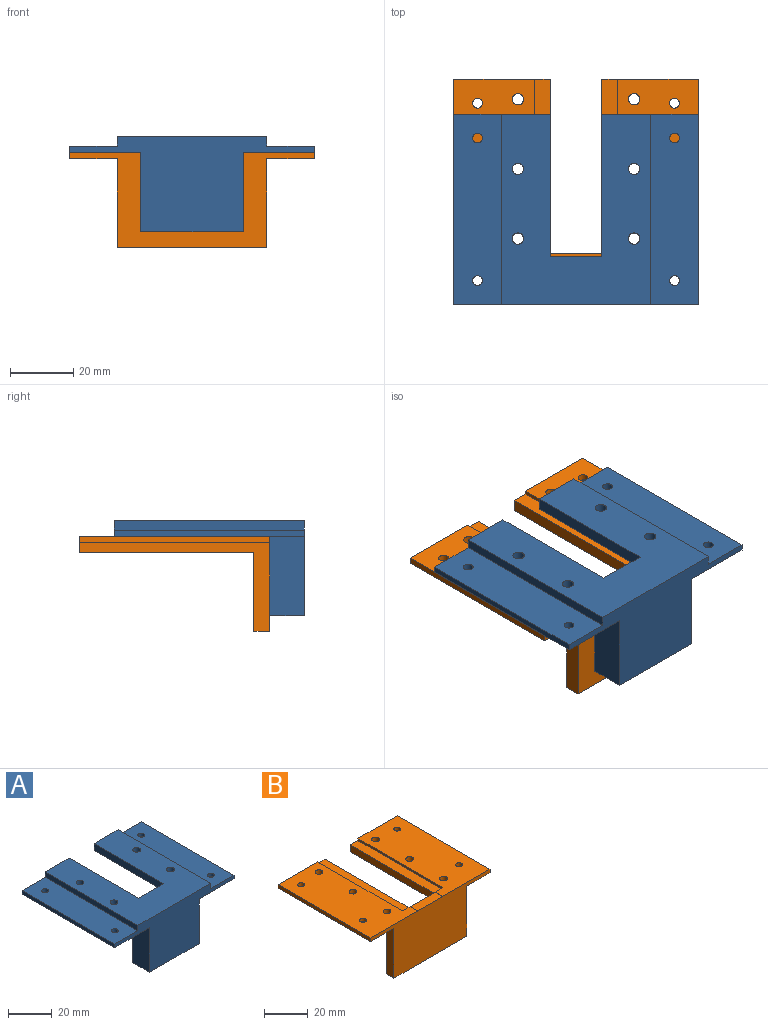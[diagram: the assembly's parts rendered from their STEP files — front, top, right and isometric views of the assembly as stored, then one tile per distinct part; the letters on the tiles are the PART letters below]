
ASSEMBLY  parts=2 mates=1
PART A: 33 faces, bbox 77.2x60x30 mm
  f0: plane 60x3mm, normal (-1,0,0), area 180mm2, adj f4,f5,f7,f29
  f1: plane 60x3mm, normal (1,0,0), area 180mm2, adj f4,f6,f7,f25
  f2: plane 60x25.5mm, normal (0,0,-1), area 1461.5mm2, adj f6,f7,f8,f15,f18,f21,f22,f26
  f3: plane 60x25.5mm, normal (0,0,-1), area 1461.5mm2, adj f5,f7,f10,f16,f17,f23,f24,f30
  f4: plane 60x47.2mm, normal (0,0,1), area 2062.3mm2, adj f0,f1,f5,f6,f7,f12,f13,f14
  f5: plane 30.5x5mm, normal (0,1,0), area 102mm2, adj f0,f3,f4,f10,f11,f14,f29,f30
  f6: plane 30.5x5mm, normal (0,1,0), area 102mm2, adj f1,f2,f4,f8,f11,f12,f25,f26
  f7: plane 77.2x30mm, normal (0,-1,0), area 1101mm2, adj f0,f1,f2,f3,f4,f19,f22,f23
  f8: plane 59x26.1mm, normal (-1,0,0), area 192.5mm2, adj f2,f6,f9,f11,f19,f20,f21
  f9: plane 26.2x1.1mm, normal (0,1,0), area 28.8mm2, adj f8,f10,f11,f20
  f10: plane 59x26.1mm, normal (1,0,0), area 192.5mm2, adj f3,f5,f9,f11,f19,f20,f24
  f11: plane 50x26.2mm, normal (0,0,-1), area 581mm2, adj f5,f6,f8,f9,f10,f12,f13,f14
  f12: plane 45x3.9mm, normal (-1,0,0), area 175.5mm2, adj f4,f6,f11,f13
  f13: plane 16.2x3.9mm, normal (0,1,0), area 63.2mm2, adj f4,f11,f12,f14
  f14: plane 45x3.9mm, normal (1,0,0), area 175.5mm2, adj f4,f5,f11,f13
  f15: cylinder r=1.8mm len=5mm, axis (0,0,-1), area 56.5mm2, adj f2,f4
  f16: cylinder r=1.8mm len=5mm, axis (0,0,-1), area 56.5mm2, adj f3,f4
  f17: cylinder r=1.8mm len=5mm, axis (0,0,-1), area 56.5mm2, adj f3,f4
  f18: cylinder r=1.8mm len=5mm, axis (0,0,-1), area 56.5mm2, adj f2,f4
  f19: plane 32.2x11mm, normal (0,0,-1), area 92.2mm2, adj f7,f8,f10,f20,f21,f22,f23,f24
  f20: plane 26.2x25mm, normal (0,0.94,-0.34), area 696.2mm2, adj f8,f9,f10,f19
  f21: plane 25x3mm, normal (0,1,0), area 75mm2, adj f2,f8,f19,f22
  f22: plane 25x11mm, normal (1,0,0), area 275mm2, adj f2,f7,f19,f21
  f23: plane 25x11mm, normal (-1,0,0), area 275mm2, adj f3,f7,f19,f24
  f24: plane 25x3mm, normal (0,1,0), area 75mm2, adj f3,f10,f19,f23
  f25: plane 60x15mm, normal (0,0,1), area 884.9mm2, adj f1,f6,f7,f26,f27,f28
  f26: plane 60x2mm, normal (1,0,0), area 120mm2, adj f2,f6,f7,f25
  f27: cylinder r=1.55mm len=3.1mm, axis (0,0,1), area 19.5mm2, adj f2,f25
  f28: cylinder r=1.55mm len=3.1mm, axis (0,0,1), area 19.5mm2, adj f2,f25
  f29: plane 60x15mm, normal (0,0,1), area 884.9mm2, adj f0,f5,f7,f30,f31,f32
  f30: plane 60x2mm, normal (-1,0,0), area 120mm2, adj f3,f5,f7,f29
  f31: cylinder r=1.55mm len=3.1mm, axis (0,0,1), area 19.5mm2, adj f3,f29
  f32: cylinder r=1.55mm len=3.1mm, axis (0,0,1), area 19.5mm2, adj f3,f29
PART B: 76 faces, bbox 77.2x60x30 mm
  f0: plane 60x28mm, normal (1,0,0), area 305mm2, adj f4,f12,f15,f17,f64,f72
  f1: plane 60x28mm, normal (-1,0,0), area 305mm2, adj f3,f14,f15,f17,f64,f68
  f2: plane 60x30.5mm, normal (0,0,1), area 1509.4mm2, adj f5,f6,f7,f14,f15,f16,f17,f66
  f3: plane 55x15.5mm, normal (0,0,-1), area 742.7mm2, adj f1,f14,f17,f20,f44,f45,f46,f47
  f4: plane 55x15.5mm, normal (0,0,-1), area 742.7mm2, adj f0,f12,f17,f21,f22,f23,f24,f25
  f5: cylinder r=1.8mm len=3.6mm, axis (0,0,1), area 28.3mm2, adj f2,f57
  f6: cylinder r=1.8mm len=3.6mm, axis (0,0,1), area 28.3mm2, adj f2,f50
  f7: cylinder r=1.8mm len=3.6mm, axis (0,0,1), area 28.3mm2, adj f2,f43
  f8: cylinder r=1.8mm len=3.6mm, axis (0,0,1), area 28.3mm2, adj f11,f42
  f9: cylinder r=1.8mm len=3.6mm, axis (0,0,1), area 28.3mm2, adj f11,f35
  f10: cylinder r=1.8mm len=3.6mm, axis (0,0,1), area 28.3mm2, adj f11,f28
  f11: plane 60x30.5mm, normal (0,0,1), area 1509.4mm2, adj f8,f9,f10,f12,f15,f17,f18,f65
  f12: plane 30.5x5mm, normal (0,1,0), area 102mm2, adj f0,f4,f11,f13,f18,f21,f72,f73
  f13: plane 55x5mm, normal (0,0,1), area 275mm2, adj f12,f17,f18,f21
  f14: plane 30.5x5mm, normal (0,1,0), area 102mm2, adj f1,f2,f3,f16,f19,f20,f68,f69
  f15: plane 77.2x30mm, normal (0,-1,0), area 1474.4mm2, adj f0,f1,f2,f11,f64,f65,f66,f67
  f16: plane 55x1.1mm, normal (1,0,0), area 60.5mm2, adj f2,f14,f17,f19
  f17: plane 47.2x30mm, normal (0,1,0), area 1270.4mm2, adj f0,f1,f2,f3,f4,f11,f13,f16
  f18: plane 55x1.1mm, normal (-1,0,0), area 60.5mm2, adj f11,f12,f13,f17
  f19: plane 55x5mm, normal (0,0,1), area 275mm2, adj f14,f16,f17,f20
  f20: plane 55x3.9mm, normal (1,0,0), area 214.5mm2, adj f3,f14,f17,f19
  f21: plane 55x3.9mm, normal (-1,0,0), area 214.5mm2, adj f4,f12,f13,f17
  f22: plane 3.25x2.5mm, normal (0.5,-0.87,0), area 9.4mm2, adj f4,f23,f27,f28
  f23: plane 3.25x2.5mm, normal (-0.5,-0.87,0), area 9.4mm2, adj f4,f22,f24,f28
  f24: plane 3.75x2.5mm, normal (-1,0,0), area 9.4mm2, adj f4,f23,f25,f28
  f25: plane 3.25x2.5mm, normal (-0.5,0.87,0), area 9.4mm2, adj f4,f24,f26,f28
  f26: plane 3.25x2.5mm, normal (0.5,0.87,0), area 9.4mm2, adj f4,f25,f27,f28
  f27: plane 3.75x2.5mm, normal (1,0,0), area 9.4mm2, adj f4,f22,f26,f28
  f28: plane 7.51x6.5mm, normal (0,0,-1), area 26.4mm2, adj f10,f22,f23,f24,f25,f26,f27
  f29: plane 3.25x2.5mm, normal (0.5,-0.87,0), area 9.4mm2, adj f4,f30,f34,f35
  f30: plane 3.25x2.5mm, normal (-0.5,-0.87,0), area 9.4mm2, adj f4,f29,f31,f35
  f31: plane 3.75x2.5mm, normal (-1,0,0), area 9.4mm2, adj f4,f30,f32,f35
  f32: plane 3.25x2.5mm, normal (-0.5,0.87,0), area 9.4mm2, adj f4,f31,f33,f35
  f33: plane 3.25x2.5mm, normal (0.5,0.87,0), area 9.4mm2, adj f4,f32,f34,f35
  f34: plane 3.75x2.5mm, normal (1,0,0), area 9.4mm2, adj f4,f29,f33,f35
  f35: plane 7.51x6.5mm, normal (0,0,-1), area 26.4mm2, adj f9,f29,f30,f31,f32,f33,f34
  f36: plane 3.25x2.5mm, normal (0.5,-0.87,0), area 9.4mm2, adj f4,f37,f41,f42
  f37: plane 3.25x2.5mm, normal (-0.5,-0.87,0), area 9.4mm2, adj f4,f36,f38,f42
  f38: plane 3.75x2.5mm, normal (-1,0,0), area 9.4mm2, adj f4,f37,f39,f42
  f39: plane 3.25x2.5mm, normal (-0.5,0.87,0), area 9.4mm2, adj f4,f38,f40,f42
  f40: plane 3.25x2.5mm, normal (0.5,0.87,0), area 9.4mm2, adj f4,f39,f41,f42
  f41: plane 3.75x2.5mm, normal (1,0,0), area 9.4mm2, adj f4,f36,f40,f42
  f42: plane 7.51x6.5mm, normal (0,0,-1), area 26.4mm2, adj f8,f36,f37,f38,f39,f40,f41
  f43: plane 7.51x6.5mm, normal (0,0,-1), area 26.4mm2, adj f7,f44,f45,f46,f47,f48,f49
  f44: plane 3.75x2.5mm, normal (1,0,0), area 9.4mm2, adj f3,f43,f45,f49
  f45: plane 3.25x2.5mm, normal (0.5,-0.87,0), area 9.4mm2, adj f3,f43,f44,f46
  f46: plane 3.25x2.5mm, normal (-0.5,-0.87,0), area 9.4mm2, adj f3,f43,f45,f47
  f47: plane 3.75x2.5mm, normal (-1,0,0), area 9.4mm2, adj f3,f43,f46,f48
  f48: plane 3.25x2.5mm, normal (-0.5,0.87,0), area 9.4mm2, adj f3,f43,f47,f49
  f49: plane 3.25x2.5mm, normal (0.5,0.87,0), area 9.4mm2, adj f3,f43,f44,f48
  f50: plane 7.51x6.5mm, normal (0,0,-1), area 26.4mm2, adj f6,f51,f52,f53,f54,f55,f56
  f51: plane 3.25x2.5mm, normal (-0.5,0.87,0), area 9.4mm2, adj f3,f50,f52,f56
  f52: plane 3.25x2.5mm, normal (0.5,0.87,0), area 9.4mm2, adj f3,f50,f51,f53
  f53: plane 3.75x2.5mm, normal (1,0,0), area 9.4mm2, adj f3,f50,f52,f54
  f54: plane 3.25x2.5mm, normal (0.5,-0.87,0), area 9.4mm2, adj f3,f50,f53,f55
  f55: plane 3.25x2.5mm, normal (-0.5,-0.87,0), area 9.4mm2, adj f3,f50,f54,f56
  f56: plane 3.75x2.5mm, normal (-1,0,0), area 9.4mm2, adj f3,f50,f51,f55
  f57: plane 7.51x6.5mm, normal (0,0,-1), area 26.4mm2, adj f5,f58,f59,f60,f61,f62,f63
  f58: plane 3.75x2.5mm, normal (-1,0,0), area 9.4mm2, adj f3,f57,f59,f63
  f59: plane 3.25x2.5mm, normal (-0.5,0.87,0), area 9.4mm2, adj f3,f57,f58,f60
  f60: plane 3.25x2.5mm, normal (0.5,0.87,0), area 9.4mm2, adj f3,f57,f59,f61
  f61: plane 3.75x2.5mm, normal (1,0,0), area 9.4mm2, adj f3,f57,f60,f62
  f62: plane 3.25x2.5mm, normal (0.5,-0.87,0), area 9.4mm2, adj f3,f57,f61,f63
  f63: plane 3.25x2.5mm, normal (-0.5,-0.87,0), area 9.4mm2, adj f3,f57,f58,f62
  f64: plane 47.2x5mm, normal (0,0,-1), area 236mm2, adj f0,f1,f15,f17
  f65: plane 5x0.1mm, normal (-1,0,0), area 0.5mm2, adj f11,f15,f17,f67
  f66: plane 5x0.1mm, normal (1,0,0), area 0.5mm2, adj f2,f15,f17,f67
  f67: plane 16.2x5mm, normal (0,0,1), area 81mm2, adj f15,f17,f65,f66
  f68: plane 60x15mm, normal (0,0,-1), area 884.9mm2, adj f1,f14,f15,f69,f70,f71
  f69: plane 60x2mm, normal (-1,0,0), area 120mm2, adj f2,f14,f15,f68
  f70: cylinder r=1.55mm len=3.1mm, axis (0,0,1), area 19.5mm2, adj f2,f68
  f71: cylinder r=1.55mm len=3.1mm, axis (0,0,1), area 19.5mm2, adj f2,f68
  f72: plane 60x15mm, normal (0,0,-1), area 884.9mm2, adj f0,f12,f15,f73,f74,f75
  f73: plane 60x2mm, normal (1,0,0), area 120mm2, adj f11,f12,f15,f72
  f74: cylinder r=1.55mm len=3.1mm, axis (0,0,1), area 19.5mm2, adj f11,f72
  f75: cylinder r=1.55mm len=3.1mm, axis (0,0,1), area 19.5mm2, adj f11,f72
PLACE A t=(-13.01,-9.36,7.22)mm
PLACE B t=(-13.01,1.64,2.22)mm
MATE fastened B.f10 <-> A.f15  axis (0,0,1) through (5.34,-18.61,7.22)mm
